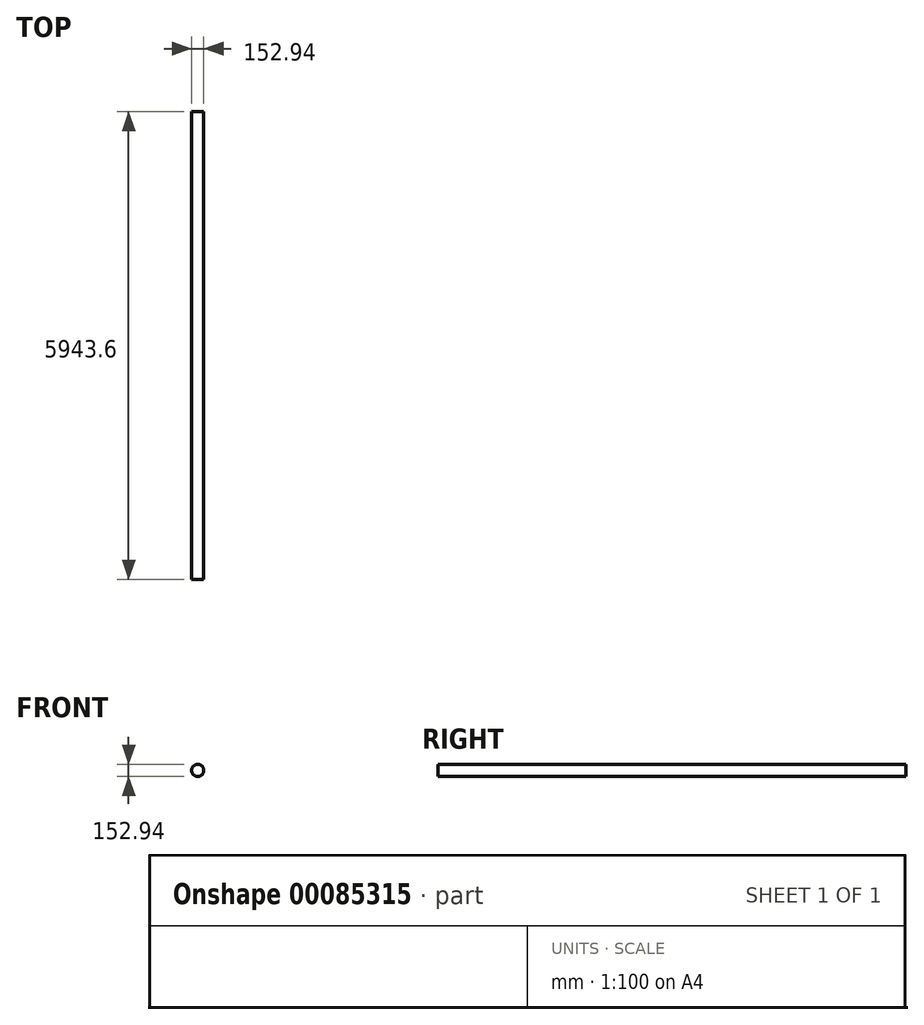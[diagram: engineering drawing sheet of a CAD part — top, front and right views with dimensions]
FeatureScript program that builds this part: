
annotation { "Feature Type Name" : "Feature", "Feature Type Description" : "" }
export const myFeature = defineFeature(function(context is Context, id is Id, definition is map)
    precondition{}
    {
        {
            var Q0;
            Q0=qCreatedBy(makeId("Front.planeOp"),FACE);
            var sketch = newSketch(context, id + "F0", { "sketchPlane" : qUnion([Q0])});
            skCircle(sketch, "E0", {"center": v(0, 0) * mm, "radius": 76.47 * mm});
            skSolve(sketch);
        }
        {
            var Q0;
            Q0 = qSketchRegion(id + "F0", true);
            extrude(context, id + "F1", {"entities" : qUnion([Q0]), "depth" : 5943.6 * mm});
        }
    });
